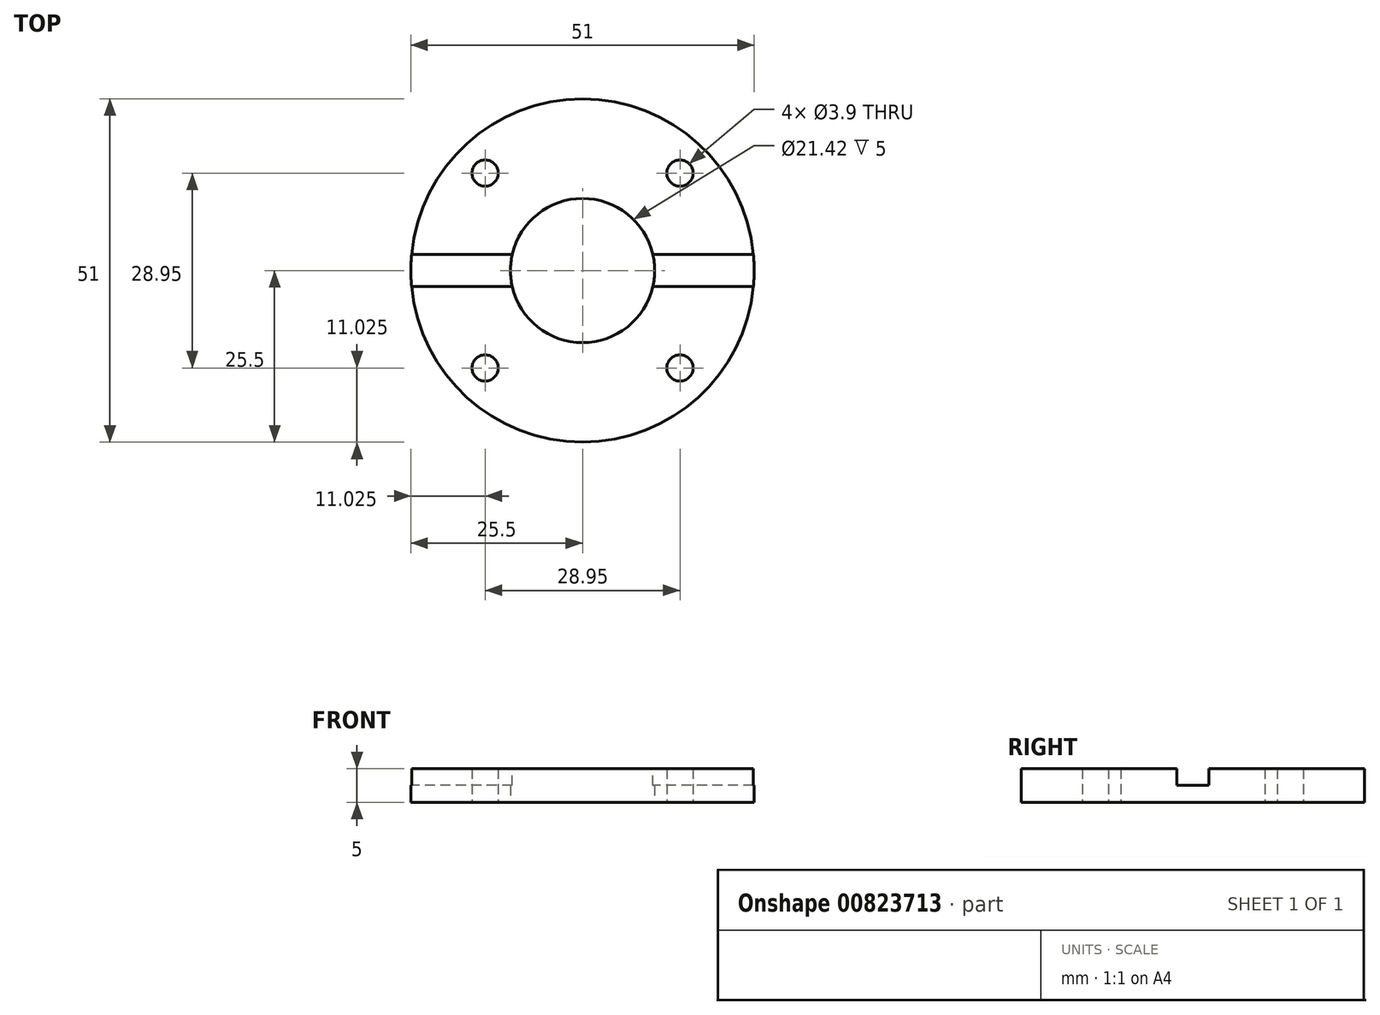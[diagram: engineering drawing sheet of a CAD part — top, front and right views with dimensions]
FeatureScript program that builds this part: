
annotation { "Feature Type Name" : "Feature", "Feature Type Description" : "" }
export const myFeature = defineFeature(function(context is Context, id is Id, definition is map)
    precondition{}
    {
        {
            var Q0;
            Q0=qCreatedBy(makeId("Top.planeOp"),FACE);
            var sketch = newSketch(context, id + "F0", { "sketchPlane" : qUnion([Q0])});
            skCircle(sketch, "E0", {"center": v(0, 0) * mm, "radius": 25.5 * mm});
            skCircle(sketch, "E1", {"center": v(0, 0) * mm, "radius": 10.71 * mm});
            skLineSegment(sketch, "E2", {"start": v(-25.5, 0) * mm, "end": v(25.5, 0) * mm, "construction": true});
            skCircle(sketch, "E3", {"center": v(14.48, -14.48) * mm, "radius": 1.95 * mm});
            skLineSegment(sketch, "E4", {"start": v(0, 25.5) * mm, "end": v(0, -25.5) * mm, "construction": true});
            skCircle(sketch, "E5.1.0", {"center": v(14.48, 14.48) * mm, "radius": 1.95 * mm});
            skCircle(sketch, "E5.2.0", {"center": v(-14.48, 14.48) * mm, "radius": 1.95 * mm});
            skCircle(sketch, "E5.3.0", {"center": v(-14.48, -14.48) * mm, "radius": 1.95 * mm});
            skSolve(sketch);
        }
        {
            var Q0;
            Q0=makeQuery(id+"F0.imprint","IMPRINT",FACE,{"disambiguationData":[TD([[makeQuery(id+"F0.imprint","IMPRINT",EDGE,{"derivedFrom":sQuery(id+"F0.wireOp",EDGE,"E0")}),1.0]])]});
            extrude(context, id + "F1", {"entities" : qUnion([Q0]), "depth" : 5 * mm, "offsetDistance" : 25 * mm});
        }
        {
            var Q0;
            Q0=makeQuery(id+"F1.opExtrude","CAP_FACE",FACE,{"disambiguationData":[OSD([sQuery(id+"F0.wireOp",EDGE,"E0"),sQuery(id+"F0.wireOp",EDGE,"E1")])],"isStart":false});
            var sketch = newSketch(context, id + "F2", { "sketchPlane" : qUnion([Q0])});
            skLineSegment(sketch, "E6.bottom", {"start": v(25.5, 2.4) * mm, "end": v(-25.5, 2.4) * mm});
            skLineSegment(sketch, "E6.top", {"start": v(25.5, -2.4) * mm, "end": v(-25.5, -2.4) * mm});
            skLineSegment(sketch, "E6.left", {"start": v(25.5, 2.4) * mm, "end": v(25.5, -2.4) * mm});
            skLineSegment(sketch, "E6.right", {"start": v(-25.5, 2.4) * mm, "end": v(-25.5, -2.4) * mm});
            skPoint(sketch, "E6.middle", {"position": v(0, 0) * mm});
            skSolve(sketch);
        }
        {
            var Q0;
            {var subQ1=makeQuery(id+"F1.opExtrude","CAP_EDGE",EDGE,{"disambiguationData":[OSD([sQuery(id+"F0.wireOp",EDGE,"E0")])],"isStart":false});var subQ6=sQuery(id+"F2.wireOp",EDGE,"E6.bottom");var subQ7=makeQuery(id+"F2.imprint","INTERSECT",VERTEX,{"disambiguationData":[OD(1.0)],"derivedFrom":[subQ1,subQ6]});Q0=makeQuery(id+"F2.imprint","IMPRINT",FACE,{"disambiguationData":[TD([[makeQuery(id+"F2.imprint","IMPRINT",EDGE,{"disambiguationData":[TD([[subQ7,1.0]])],"derivedFrom":subQ6}),1.0]])]});}
            var Q1;
            {var subQ1=makeQuery(id+"F1.opExtrude","CAP_EDGE",EDGE,{"disambiguationData":[OSD([sQuery(id+"F0.wireOp",EDGE,"E0")])],"isStart":false});var subQ4=sQuery(id+"F2.wireOp",EDGE,"E6.bottom");var subQ5=makeQuery(id+"F2.imprint","INTERSECT",VERTEX,{"disambiguationData":[OD(0.0)],"derivedFrom":[subQ1,subQ4]});Q1=makeQuery(id+"F2.imprint","IMPRINT",FACE,{"disambiguationData":[TD([[makeQuery(id+"F2.imprint","IMPRINT",EDGE,{"disambiguationData":[TD([[subQ5,-1.0]])],"derivedFrom":subQ4}),1.0]])]});}
            extrude(context, id + "F3", {"entities" : qUnion([Q0, Q1]), "operationType" : NewBodyOperationType.REMOVE, "oppositeDirection" : true, "depth" : 2.5 * mm, "offsetDistance" : 25 * mm});
        }
    });
